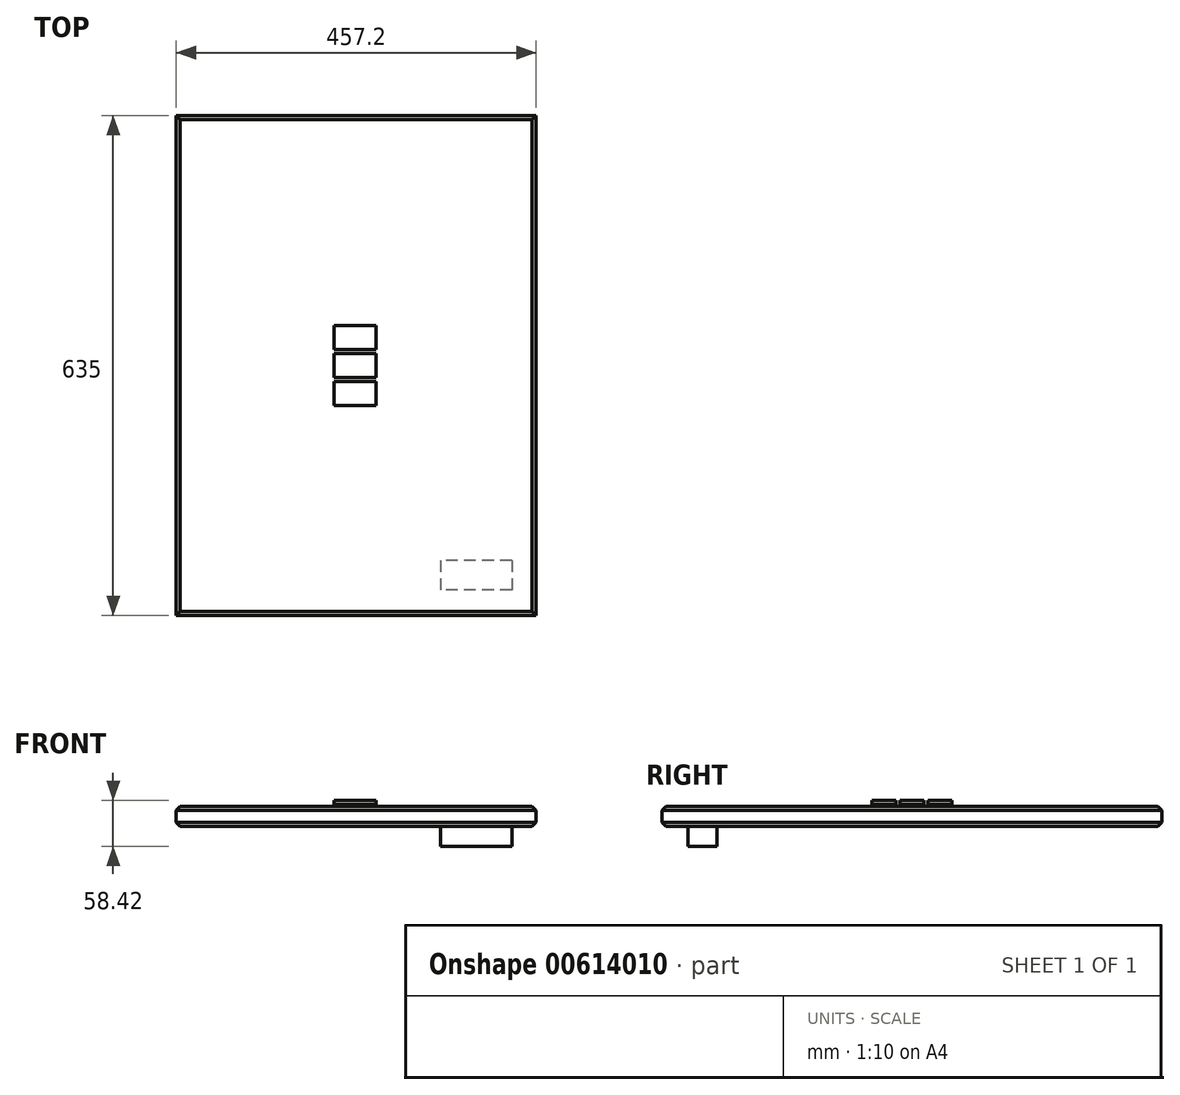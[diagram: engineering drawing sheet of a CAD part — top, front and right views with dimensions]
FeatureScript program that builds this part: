
annotation { "Feature Type Name" : "Feature", "Feature Type Description" : "" }
export const myFeature = defineFeature(function(context is Context, id is Id, definition is map)
    precondition{}
    {
        {
            var Q0;
            Q0=qCreatedBy(makeId("Top.planeOp"),FACE);
            var sketch = newSketch(context, id + "F0", { "sketchPlane" : qUnion([Q0])});
            skLineSegment(sketch, "E0.bottom", {"start": v(-228.6, 317.5) * mm, "end": v(228.6, 317.5) * mm});
            skLineSegment(sketch, "E0.top", {"start": v(-228.6, -317.5) * mm, "end": v(228.6, -317.5) * mm});
            skLineSegment(sketch, "E0.left", {"start": v(-228.6, 317.5) * mm, "end": v(-228.6, -317.5) * mm});
            skLineSegment(sketch, "E0.right", {"start": v(228.6, 317.5) * mm, "end": v(228.6, -317.5) * mm});
            skPoint(sketch, "E0.middle", {"position": v(0, 0) * mm});
            skSolve(sketch);
        }
        {
            var Q0;
            Q0=qSketchRegion(id+"F0",true);
            extrude(context, id + "F1", {"entities" : qUnion([Q0]), "depth" : 25.4 * mm, "offsetDistance" : 25.4 * mm});
        }
        {
            var Q0;
            Q0=makeQuery(id+"F1.opExtrude","CAP_EDGE",EDGE,{"disambiguationData":[OSD([sQuery(id+"F0.wireOp",EDGE,"E0.top")])],"isStart":false});
            var Q1;
            Q1=makeQuery(id+"F1.opExtrude","CAP_EDGE",EDGE,{"disambiguationData":[OSD([sQuery(id+"F0.wireOp",EDGE,"E0.left")])],"isStart":false});
            var Q2;
            Q2=makeQuery(id+"F1.opExtrude","CAP_EDGE",EDGE,{"disambiguationData":[OSD([sQuery(id+"F0.wireOp",EDGE,"E0.bottom")])],"isStart":false});
            var Q3;
            Q3=makeQuery(id+"F1.opExtrude","CAP_EDGE",EDGE,{"disambiguationData":[OSD([sQuery(id+"F0.wireOp",EDGE,"E0.right")])],"isStart":false});
            var Q4;
            Q4=makeQuery(id+"F1.opExtrude","CAP_EDGE",EDGE,{"disambiguationData":[OSD([sQuery(id+"F0.wireOp",EDGE,"E0.right")])],"isStart":true});
            var Q5;
            Q5=makeQuery(id+"F1.opExtrude","CAP_EDGE",EDGE,{"disambiguationData":[OSD([sQuery(id+"F0.wireOp",EDGE,"E0.top")])],"isStart":true});
            var Q6;
            Q6=makeQuery(id+"F1.opExtrude","CAP_EDGE",EDGE,{"disambiguationData":[OSD([sQuery(id+"F0.wireOp",EDGE,"E0.left")])],"isStart":true});
            var Q7;
            Q7=makeQuery(id+"F1.opExtrude","CAP_EDGE",EDGE,{"disambiguationData":[OSD([sQuery(id+"F0.wireOp",EDGE,"E0.bottom")])],"isStart":true});
            chamfer(context, id + "F2", {"entities" : qUnion([Q0, Q1, Q2, Q3, Q4, Q5, Q6, Q7]), "width" : 5.08 * mm, "tangentPropagation" : true});
        }
        {
            var Q0;
            Q0=makeQuery(id+"F1.opExtrude","CAP_FACE",FACE,{"disambiguationData":[OSD([sQuery(id+"F0.wireOp",EDGE,"E0.bottom"),sQuery(id+"F0.wireOp",EDGE,"E0.top"),sQuery(id+"F0.wireOp",EDGE,"E0.left"),sQuery(id+"F0.wireOp",EDGE,"E0.right")])],"isStart":true});
            var sketch = newSketch(context, id + "F3", { "sketchPlane" : qUnion([Q0])});
            skLineSegment(sketch, "E1.bottom", {"start": v(197.87, 247.58) * mm, "end": v(107.2, 247.58) * mm});
            skLineSegment(sketch, "E1.top", {"start": v(197.87, 284.92) * mm, "end": v(107.2, 284.92) * mm});
            skLineSegment(sketch, "E1.left", {"start": v(197.87, 247.58) * mm, "end": v(197.87, 284.92) * mm});
            skLineSegment(sketch, "E1.right", {"start": v(107.2, 247.58) * mm, "end": v(107.2, 284.92) * mm});
            skSolve(sketch);
        }
        {
            var Q0;
            Q0=makeQuery(id+"F3.imprint","IMPRINT",FACE,{"disambiguationData":[TD([[makeQuery(id+"F3.imprint","IMPRINT",EDGE,{"derivedFrom":sQuery(id+"F3.wireOp",EDGE,"E1.bottom")}),-1.0]])]});
            extrude(context, id + "F4", {"entities" : qUnion([Q0]), "operationType" : NewBodyOperationType.ADD, "depth" : 25.4 * mm, "offsetDistance" : 25.4 * mm});
        }
        {
            var Q0;
            Q0=qCreatedBy(makeId("Top.planeOp"),FACE);
            var sketch = newSketch(context, id + "F5", { "sketchPlane" : qUnion([Q0])});
            skLineSegment(sketch, "E2.bottom", {"start": v(-698.37, 114.43) * mm, "end": v(-751.7, 114.43) * mm});
            skLineSegment(sketch, "E2.top", {"start": v(-698.37, 144.91) * mm, "end": v(-751.7, 144.91) * mm});
            skLineSegment(sketch, "E2.left", {"start": v(-698.37, 114.43) * mm, "end": v(-698.37, 144.91) * mm});
            skLineSegment(sketch, "E2.right", {"start": v(-751.7, 114.43) * mm, "end": v(-751.7, 144.91) * mm});
            skPoint(sketch, "E2.middle", {"position": v(-725.04, 129.67) * mm});
            skSolve(sketch);
        }
        {
            var Q0;
            Q0=qSketchRegion(id+"F5",true);
            extrude(context, id + "F6", {"entities" : qUnion([Q0]), "depth" : 5.08 * mm, "offsetDistance" : 25.4 * mm});
        }
        {
            var Q0;
            Q0=makeQuery(id+"F6.opExtrude","SWEPT_BODY",BODY,{"disambiguationData":[OSD([sQuery(id+"F5.wireOp",EDGE,"E2.bottom"),sQuery(id+"F5.wireOp",EDGE,"E2.top"),sQuery(id+"F5.wireOp",EDGE,"E2.left"),sQuery(id+"F5.wireOp",EDGE,"E2.right")])]});
            transform(context, id + "F7", {"entities" : qUnion([Q0]), "transformType" : TransformType.TRANSLATION_3D, "dx" : 0 * mm, "dy" : 203.2 * mm, "dz" : 0 * mm, "makeCopy" : true});
        }
        {
            var Q0;
            Q0=makeQuery(id+"F6.opExtrude","SWEPT_BODY",BODY,{"disambiguationData":[OSD([sQuery(id+"F5.wireOp",EDGE,"E2.bottom"),sQuery(id+"F5.wireOp",EDGE,"E2.top"),sQuery(id+"F5.wireOp",EDGE,"E2.left"),sQuery(id+"F5.wireOp",EDGE,"E2.right")])]});
            transform(context, id + "F8", {"entities" : qUnion([Q0]), "transformType" : TransformType.TRANSLATION_3D, "dx" : 0 * mm, "dy" : -203.2 * mm, "dz" : 0 * mm, "makeCopy" : true});
        }
        {
            var Q0;
            Q0=makeQuery(id+"F8.opPattern","COPY",BODY,{"derivedFrom":makeQuery(id+"F6.opExtrude","SWEPT_BODY",BODY,{"disambiguationData":[OSD([sQuery(id+"F5.wireOp",EDGE,"E2.bottom"),sQuery(id+"F5.wireOp",EDGE,"E2.top"),sQuery(id+"F5.wireOp",EDGE,"E2.left"),sQuery(id+"F5.wireOp",EDGE,"E2.right")])]}),"instanceName":"1"});
            var Q1;
            Q1=makeQuery(id+"F7.opPattern","COPY",BODY,{"derivedFrom":makeQuery(id+"F6.opExtrude","SWEPT_BODY",BODY,{"disambiguationData":[OSD([sQuery(id+"F5.wireOp",EDGE,"E2.bottom"),sQuery(id+"F5.wireOp",EDGE,"E2.top"),sQuery(id+"F5.wireOp",EDGE,"E2.left"),sQuery(id+"F5.wireOp",EDGE,"E2.right")])]}),"instanceName":"1"});
            var Q2;
            Q2=makeQuery(id+"F6.opExtrude","SWEPT_BODY",BODY,{"disambiguationData":[OSD([sQuery(id+"F5.wireOp",EDGE,"E2.bottom"),sQuery(id+"F5.wireOp",EDGE,"E2.top"),sQuery(id+"F5.wireOp",EDGE,"E2.left"),sQuery(id+"F5.wireOp",EDGE,"E2.right")])]});
            transform(context, id + "F9", {"entities" : qUnion([Q0, Q1, Q2]), "transformType" : TransformType.TRANSLATION_3D, "dx" : 723.9 * mm, "dy" : -129.54 * mm, "dz" : 27.94 * mm, "makeCopy" : false});
        }
        {
            var Q0;
            Q0=makeQuery(id+"F7.opPattern","COPY",BODY,{"derivedFrom":makeQuery(id+"F6.opExtrude","SWEPT_BODY",BODY,{"disambiguationData":[OSD([sQuery(id+"F5.wireOp",EDGE,"E2.bottom"),sQuery(id+"F5.wireOp",EDGE,"E2.top"),sQuery(id+"F5.wireOp",EDGE,"E2.left"),sQuery(id+"F5.wireOp",EDGE,"E2.right")])]}),"instanceName":"1"});
            transform(context, id + "F10", {"entities" : qUnion([Q0]), "transformType" : TransformType.TRANSLATION_3D, "dx" : 0 * mm, "dy" : -167.64 * mm, "dz" : 0 * mm, "makeCopy" : false});
        }
        {
            var Q0;
            Q0=makeQuery(id+"F8.opPattern","COPY",BODY,{"derivedFrom":makeQuery(id+"F6.opExtrude","SWEPT_BODY",BODY,{"disambiguationData":[OSD([sQuery(id+"F5.wireOp",EDGE,"E2.bottom"),sQuery(id+"F5.wireOp",EDGE,"E2.top"),sQuery(id+"F5.wireOp",EDGE,"E2.left"),sQuery(id+"F5.wireOp",EDGE,"E2.right")])]}),"instanceName":"1"});
            transform(context, id + "F11", {"entities" : qUnion([Q0]), "transformType" : TransformType.TRANSLATION_3D, "dx" : 0 * mm, "dy" : 167.64 * mm, "dz" : 0 * mm, "makeCopy" : false});
        }
    });
